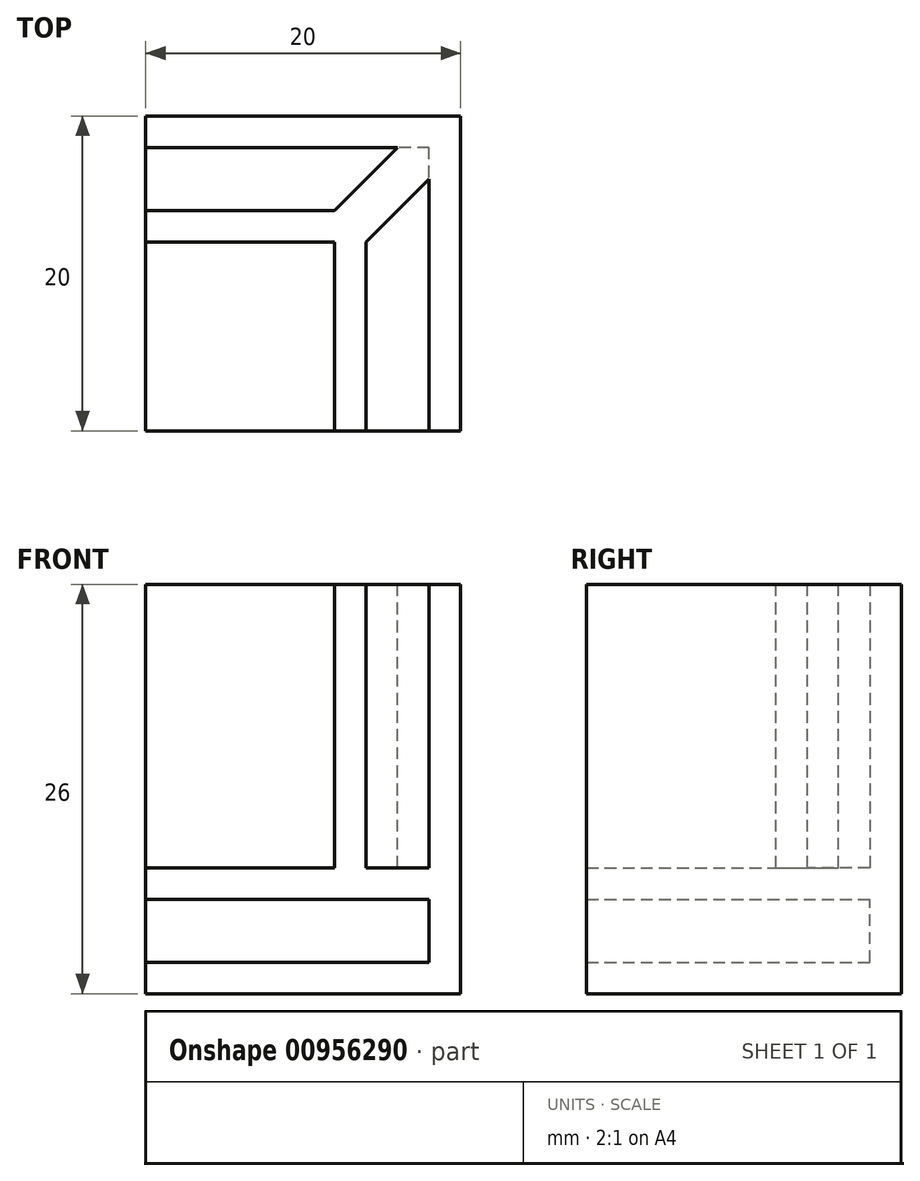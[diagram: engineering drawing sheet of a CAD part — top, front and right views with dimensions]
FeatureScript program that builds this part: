
annotation { "Feature Type Name" : "Feature", "Feature Type Description" : "" }
export const myFeature = defineFeature(function(context is Context, id is Id, definition is map)
    precondition{}
    {
        {
            var Q0;
            Q0=qCreatedBy(makeId("Top.planeOp"),FACE);
            var sketch = newSketch(context, id + "F0", { "sketchPlane" : qUnion([Q0])});
            skLineSegment(sketch, "E0.bottom", {"start": v(0, 0) * mm, "end": v(20, 0) * mm});
            skLineSegment(sketch, "E0.top", {"start": v(0, 20) * mm, "end": v(20, 20) * mm});
            skLineSegment(sketch, "E0.left", {"start": v(0, 0) * mm, "end": v(0, 20) * mm});
            skLineSegment(sketch, "E0.right", {"start": v(20, 0) * mm, "end": v(20, 20) * mm});
            skSolve(sketch);
        }
        {
            var Q0;
            Q0=makeQuery(id+"F0.imprint","IMPRINT",FACE,{"disambiguationData":[TD([[makeQuery(id+"F0.imprint","IMPRINT",EDGE,{"derivedFrom":sQuery(id+"F0.wireOp",EDGE,"E0.bottom")}),1.0]])]});
            extrude(context, id + "F1", {"entities" : qUnion([Q0]), "depth" : 26 * mm, "offsetDistance" : 25 * mm});
        }
        {
            var Q0;
            Q0=makeQuery(id+"F1.opExtrude","SWEPT_FACE",FACE,{"disambiguationData":[OSD([sQuery(id+"F0.wireOp",EDGE,"E0.left")])]});
            var sketch = newSketch(context, id + "F2", { "sketchPlane" : qUnion([Q0])});
            skLineSegment(sketch, "E1.bottom", {"start": v(0, 26) * mm, "end": v(-12, 26) * mm});
            skLineSegment(sketch, "E1.top", {"start": v(0, 8) * mm, "end": v(-12, 8) * mm});
            skLineSegment(sketch, "E1.left", {"start": v(0, 26) * mm, "end": v(0, 8) * mm});
            skLineSegment(sketch, "E1.right", {"start": v(-12, 26) * mm, "end": v(-12, 8) * mm});
            skSolve(sketch);
        }
        {
            var Q0;
            Q0=makeQuery(id+"F2.imprint","IMPRINT",FACE,{"disambiguationData":[TD([[makeQuery(id+"F2.imprint","IMPRINT",EDGE,{"derivedFrom":sQuery(id+"F2.wireOp",EDGE,"E1.bottom")}),1.0]])]});
            extrude(context, id + "F3", {"entities" : qUnion([Q0]), "operationType" : NewBodyOperationType.REMOVE, "oppositeDirection" : true, "depth" : 12 * mm, "offsetDistance" : 25 * mm});
        }
        {
            var Q0;
            Q0=makeQuery(id+"F1.opExtrude","SWEPT_FACE",FACE,{"disambiguationData":[OSD([sQuery(id+"F0.wireOp",EDGE,"E0.left")])]});
            var sketch = newSketch(context, id + "F4", { "sketchPlane" : qUnion([Q0])});
            skLineSegment(sketch, "E2.bottom", {"start": v(0, 2) * mm, "end": v(-18, 2) * mm});
            skLineSegment(sketch, "E2.top", {"start": v(0, 6) * mm, "end": v(-18, 6) * mm});
            skLineSegment(sketch, "E2.left", {"start": v(0, 2) * mm, "end": v(0, 6) * mm});
            skLineSegment(sketch, "E2.right", {"start": v(-18, 2) * mm, "end": v(-18, 6) * mm});
            skSolve(sketch);
        }
        {
            var Q0;
            Q0=makeQuery(id+"F4.imprint","IMPRINT",FACE,{"disambiguationData":[TD([[makeQuery(id+"F4.imprint","IMPRINT",EDGE,{"derivedFrom":sQuery(id+"F4.wireOp",EDGE,"E2.bottom")}),-1.0]])]});
            extrude(context, id + "F5", {"entities" : qUnion([Q0]), "operationType" : NewBodyOperationType.REMOVE, "oppositeDirection" : true, "depth" : 18 * mm, "offsetDistance" : 25 * mm});
        }
        {
            var Q0;
            Q0=makeQuery(id+"F1.opExtrude","SWEPT_FACE",FACE,{"disambiguationData":[OSD([sQuery(id+"F0.wireOp",EDGE,"E0.left")])]});
            var sketch = newSketch(context, id + "F6", { "sketchPlane" : qUnion([Q0])});
            skLineSegment(sketch, "E3.bottom", {"start": v(-18, 26) * mm, "end": v(-14, 26) * mm});
            skLineSegment(sketch, "E3.top", {"start": v(-18, 8) * mm, "end": v(-14, 8) * mm});
            skLineSegment(sketch, "E3.left", {"start": v(-18, 26) * mm, "end": v(-18, 8) * mm});
            skLineSegment(sketch, "E3.right", {"start": v(-14, 26) * mm, "end": v(-14, 8) * mm});
            skSolve(sketch);
        }
        {
            var Q0;
            Q0=makeQuery(id+"F6.imprint","IMPRINT",FACE,{"disambiguationData":[TD([[makeQuery(id+"F6.imprint","IMPRINT",EDGE,{"derivedFrom":sQuery(id+"F6.wireOp",EDGE,"E3.bottom")}),1.0]])]});
            extrude(context, id + "F7", {"entities" : qUnion([Q0]), "operationType" : NewBodyOperationType.REMOVE, "oppositeDirection" : true, "depth" : 12 * mm, "offsetDistance" : 25 * mm});
        }
        {
            var Q0;
            Q0=makeQuery(id+"F1.opExtrude","CAP_FACE",FACE,{"disambiguationData":[OSD([sQuery(id+"F0.wireOp",EDGE,"E0.bottom"),sQuery(id+"F0.wireOp",EDGE,"E0.top"),sQuery(id+"F0.wireOp",EDGE,"E0.left"),sQuery(id+"F0.wireOp",EDGE,"E0.right")])],"isStart":false});
            var sketch = newSketch(context, id + "F8", { "sketchPlane" : qUnion([Q0])});
            skLineSegment(sketch, "E4", {"start": v(12, 12) * mm, "end": v(20, 20) * mm, "construction": true});
            skLineSegment(sketch, "E5", {"start": v(12, 14) * mm, "end": v(16, 18) * mm});
            skLineSegment(sketch, "E6", {"start": v(12, 18) * mm, "end": v(16, 18) * mm});
            skLineSegment(sketch, "E7", {"start": v(12, 18) * mm, "end": v(12, 14) * mm});
            skLineSegment(sketch, "E8.MirrorCS", {"start": v(14, 12) * mm, "end": v(18, 16) * mm});
            skLineSegment(sketch, "E9.MirrorCS", {"start": v(18, 12) * mm, "end": v(18, 16) * mm});
            skLineSegment(sketch, "E10", {"start": v(14, 12) * mm, "end": v(14, 0) * mm});
            skLineSegment(sketch, "E11", {"start": v(14, 0) * mm, "end": v(18, 0) * mm});
            skLineSegment(sketch, "E12", {"start": v(18, 0) * mm, "end": v(18, 12) * mm});
            skSolve(sketch);
        }
        {
            var Q0;
            Q0=makeQuery(id+"F8.imprint","IMPRINT",FACE,{"disambiguationData":[TD([[makeQuery(id+"F8.imprint","IMPRINT",EDGE,{"derivedFrom":sQuery(id+"F8.wireOp",EDGE,"E5")}),1.0]])]});
            var Q1;
            Q1=makeQuery(id+"F8.imprint","IMPRINT",FACE,{"disambiguationData":[TD([[makeQuery(id+"F8.imprint","IMPRINT",EDGE,{"derivedFrom":sQuery(id+"F8.wireOp",EDGE,"E8.MirrorCS")}),-1.0]])]});
            extrude(context, id + "F9", {"entities" : qUnion([Q0, Q1]), "operationType" : NewBodyOperationType.REMOVE, "oppositeDirection" : true, "depth" : 18 * mm, "offsetDistance" : 25 * mm});
        }
    });
